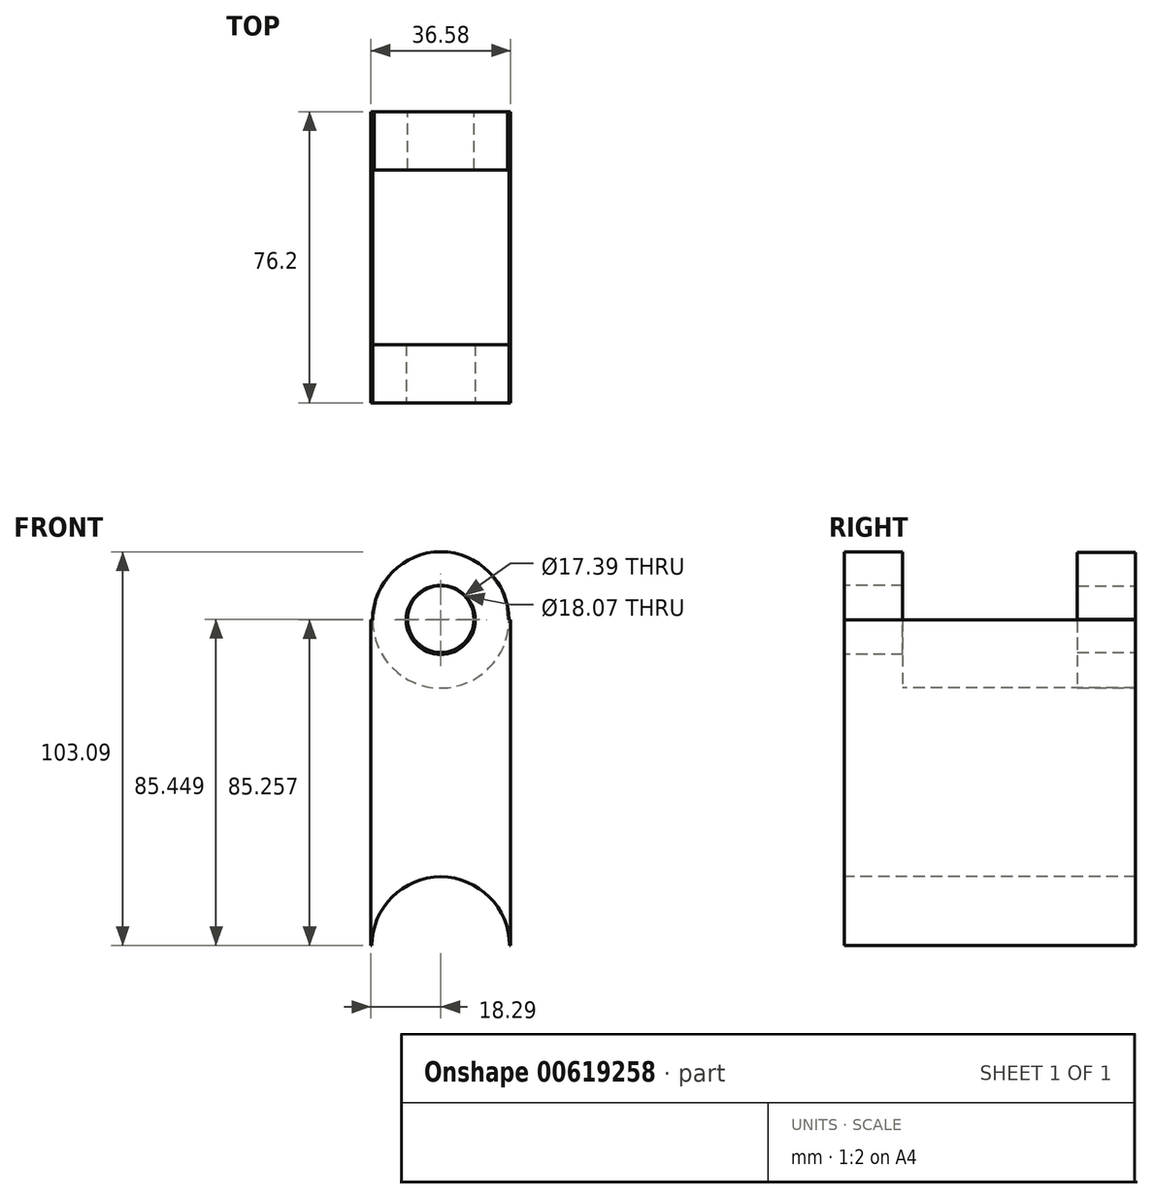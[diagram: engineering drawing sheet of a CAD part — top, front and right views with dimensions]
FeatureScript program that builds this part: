
annotation { "Feature Type Name" : "Feature", "Feature Type Description" : "" }
export const myFeature = defineFeature(function(context is Context, id is Id, definition is map)
    precondition{}
    {
        {
            var Q0;
            Q0=qCreatedBy(makeId("Front.planeOp"),FACE);
            var sketch = newSketch(context, id + "F0", { "sketchPlane" : qUnion([Q0])});
            skLineSegment(sketch, "E0.bottom", {"start": v(18.29, -42.63) * mm, "end": v(-18.29, -42.63) * mm});
            skLineSegment(sketch, "E0.top", {"start": v(18.29, 42.63) * mm, "end": v(-18.29, 42.63) * mm});
            skLineSegment(sketch, "E0.left", {"start": v(18.29, -42.63) * mm, "end": v(18.29, 42.63) * mm});
            skLineSegment(sketch, "E0.right", {"start": v(-18.29, -42.63) * mm, "end": v(-18.29, 42.63) * mm});
            skPoint(sketch, "E0.middle", {"position": v(0, 0) * mm});
            skCircle(sketch, "E1", {"center": v(0, 42.63) * mm, "radius": 17.83 * mm});
            skCircle(sketch, "E2", {"center": v(0, -42.63) * mm, "radius": 18.02 * mm});
            skCircle(sketch, "E3", {"center": v(0, 42.63) * mm, "radius": 9.03 * mm});
            skCircle(sketch, "E4", {"center": v(0, -42.63) * mm, "radius": 9.25 * mm});
            skSolve(sketch);
        }
        {
            var Q0;
            {var subQ0=sQuery(id+"F0.wireOp",EDGE,"E2");var subQ1=sQuery(id+"F0.wireOp",EDGE,"E0.bottom");var subQ2=makeQuery(id+"F0.imprint","INTERSECT",VERTEX,{"disambiguationData":[OD(0.0)],"derivedFrom":[subQ1,subQ0]});Q0=makeQuery(id+"F0.imprint","IMPRINT",FACE,{"disambiguationData":[TD([[makeQuery(id+"F0.imprint","IMPRINT",EDGE,{"disambiguationData":[TD([[subQ2,-1.0]])],"derivedFrom":subQ1}),-1.0]])]});}
            var Q1;
            {var subQ0=sQuery(id+"F0.wireOp",EDGE,"E2");var subQ1=sQuery(id+"F0.wireOp",EDGE,"E0.bottom");var subQ2=makeQuery(id+"F0.imprint","INTERSECT",VERTEX,{"disambiguationData":[OD(0.0)],"derivedFrom":[subQ1,subQ0]});Q1=makeQuery(id+"F0.imprint","IMPRINT",FACE,{"disambiguationData":[TD([[makeQuery(id+"F0.imprint","IMPRINT",EDGE,{"disambiguationData":[TD([[subQ2,-1.0]])],"derivedFrom":subQ1}),1.0]])]});}
            extrude(context, id + "F1", {"entities" : qUnion([Q0, Q1]), "oppositeDirection" : true, "depth" : 76.2 * mm, "offsetDistance" : 25.4 * mm});
        }
        {
            var Q0;
            {var subQ7=sQuery(id+"F0.wireOp",EDGE,"E0.left");Q0=makeQuery(id+"F0.imprint","IMPRINT",FACE,{"disambiguationData":[TD([[makeQuery(id+"F0.imprint","IMPRINT",EDGE,{"derivedFrom":subQ7}),1.0]])]});}
            var Q1;
            {var subQ0=sQuery(id+"F0.wireOp",EDGE,"E1");var subQ1=sQuery(id+"F0.wireOp",EDGE,"E0.top");var subQ2=makeQuery(id+"F0.imprint","INTERSECT",VERTEX,{"disambiguationData":[OD(0.0)],"derivedFrom":[subQ1,subQ0]});Q1=makeQuery(id+"F0.imprint","IMPRINT",FACE,{"disambiguationData":[TD([[makeQuery(id+"F0.imprint","IMPRINT",EDGE,{"disambiguationData":[TD([[subQ2,-1.0]])],"derivedFrom":subQ1}),-1.0]])]});}
            var Q2;
            {var subQ0=sQuery(id+"F0.wireOp",EDGE,"E1");var subQ1=sQuery(id+"F0.wireOp",EDGE,"E0.top");var subQ2=makeQuery(id+"F0.imprint","INTERSECT",VERTEX,{"disambiguationData":[OD(0.0)],"derivedFrom":[subQ1,subQ0]});Q2=makeQuery(id+"F0.imprint","IMPRINT",FACE,{"disambiguationData":[TD([[makeQuery(id+"F0.imprint","IMPRINT",EDGE,{"disambiguationData":[TD([[subQ2,-1.0]])],"derivedFrom":subQ1}),1.0]])]});}
            extrude(context, id + "F2", {"entities" : qUnion([Q0, Q1, Q2]), "operationType" : NewBodyOperationType.ADD, "oppositeDirection" : true, "depth" : 15.24 * mm, "offsetDistance" : 25.4 * mm});
        }
        {
            var Q0;
            Q0=makeQuery(id+"F1.opExtrude","CAP_FACE",FACE,{"disambiguationData":[OSD([sQuery(id+"F0.wireOp",EDGE,"E2"),sQuery(id+"F0.wireOp",EDGE,"E4")])],"isStart":false});
            var sketch = newSketch(context, id + "F3", { "sketchPlane" : qUnion([Q0])});
            skLineSegment(sketch, "E5.bottom", {"start": v(18.02, -42.82) * mm, "end": v(-18.02, -42.82) * mm});
            skLineSegment(sketch, "E5.top", {"start": v(18.02, 42.82) * mm, "end": v(-18.02, 42.82) * mm});
            skLineSegment(sketch, "E5.left", {"start": v(18.02, -42.82) * mm, "end": v(18.02, 42.82) * mm});
            skLineSegment(sketch, "E5.right", {"start": v(-18.02, -42.82) * mm, "end": v(-18.02, 42.82) * mm});
            skPoint(sketch, "E5.middle", {"position": v(0, 0) * mm});
            skCircle(sketch, "E6", {"center": v(0, 42.82) * mm, "radius": 17.48 * mm});
            skCircle(sketch, "E7", {"center": v(0, -42.82) * mm, "radius": 18.21 * mm});
            skCircle(sketch, "E8", {"center": v(0, 42.82) * mm, "radius": 8.7 * mm});
            skCircle(sketch, "E9", {"center": v(0, -42.82) * mm, "radius": 8.93 * mm});
            skSolve(sketch);
        }
        {
            var Q0;
            {var subQ0=sQuery(id+"F3.wireOp",EDGE,"E6");var subQ1=sQuery(id+"F3.wireOp",EDGE,"E5.top");var subQ2=makeQuery(id+"F3.imprint","INTERSECT",VERTEX,{"disambiguationData":[OD(0.0)],"derivedFrom":[subQ1,subQ0]});Q0=makeQuery(id+"F3.imprint","IMPRINT",FACE,{"disambiguationData":[TD([[makeQuery(id+"F3.imprint","IMPRINT",EDGE,{"disambiguationData":[TD([[subQ2,-1.0]])],"derivedFrom":subQ1}),1.0]])]});}
            var Q1;
            {var subQ0=sQuery(id+"F3.wireOp",EDGE,"E6");var subQ1=sQuery(id+"F3.wireOp",EDGE,"E5.top");var subQ2=makeQuery(id+"F3.imprint","INTERSECT",VERTEX,{"disambiguationData":[OD(0.0)],"derivedFrom":[subQ1,subQ0]});Q1=makeQuery(id+"F3.imprint","IMPRINT",FACE,{"disambiguationData":[TD([[makeQuery(id+"F3.imprint","IMPRINT",EDGE,{"disambiguationData":[TD([[subQ2,-1.0]])],"derivedFrom":subQ1}),-1.0]])]});}
            var Q2;
            {var subQ0=sQuery(id+"F3.wireOp",EDGE,"E5.left");var subQ1=sQuery(id+"F3.wireOp",EDGE,"E5.top");var subQ2=makeQuery(id+"F3.imprint","INTERSECT",VERTEX,{"derivedFrom":[subQ1,subQ0]});Q2=makeQuery(id+"F3.imprint","IMPRINT",FACE,{"disambiguationData":[TD([[makeQuery(id+"F3.imprint","IMPRINT",EDGE,{"disambiguationData":[TD([[subQ2,-1.0]])],"derivedFrom":subQ1}),1.0]])]});}
            extrude(context, id + "F4", {"entities" : qUnion([Q0, Q1, Q2]), "oppositeDirection" : true, "depth" : 15.24 * mm, "offsetDistance" : 25.4 * mm});
        }
    });
